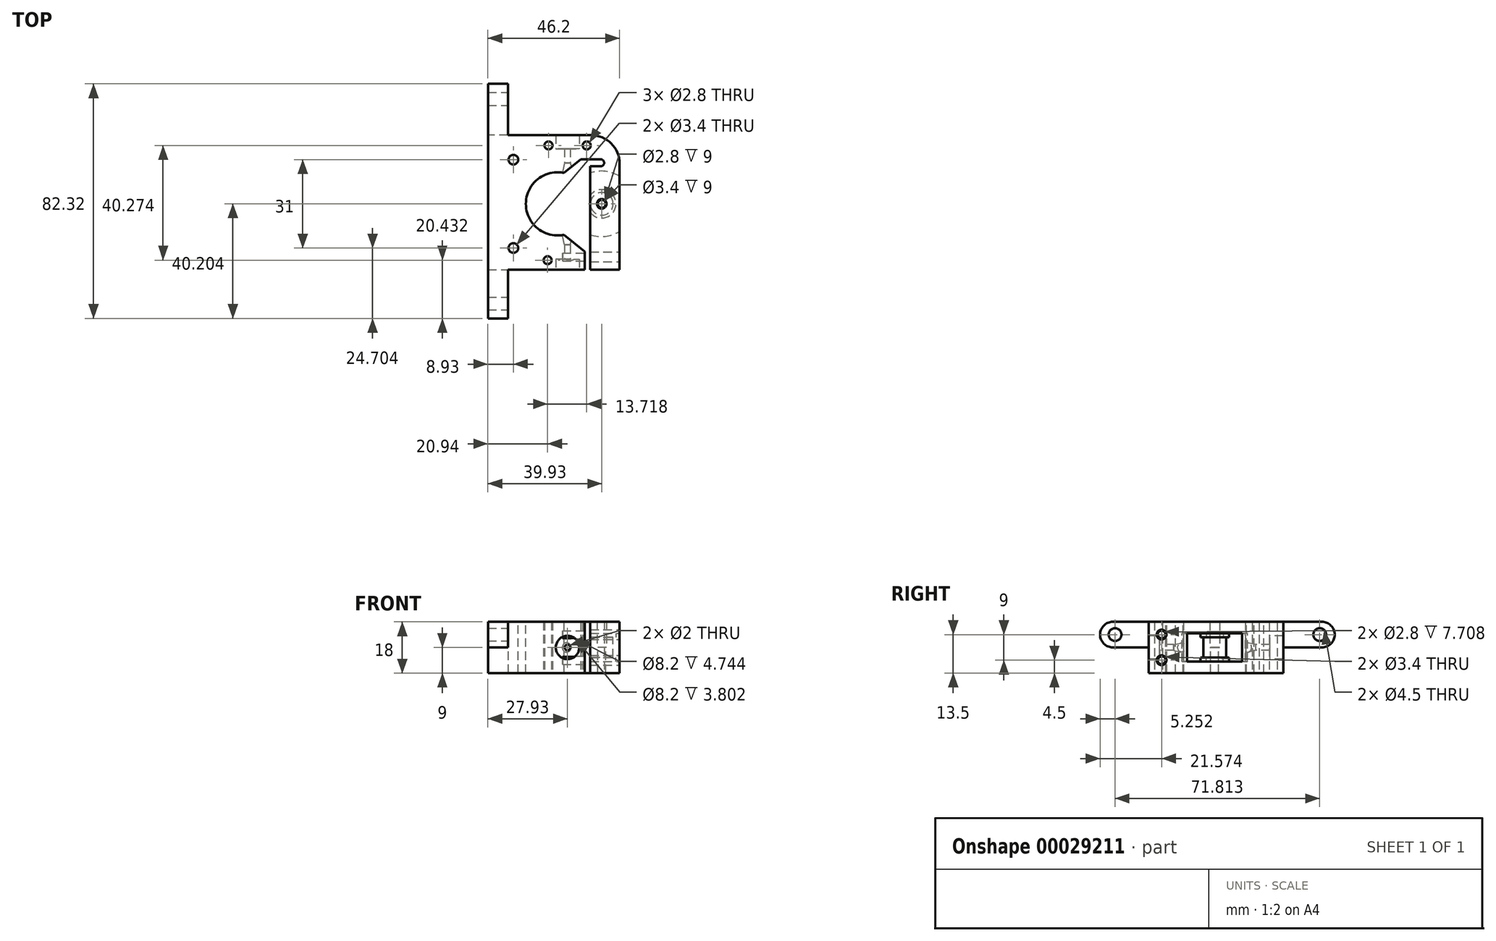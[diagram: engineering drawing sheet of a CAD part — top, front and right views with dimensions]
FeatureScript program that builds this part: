
annotation { "Feature Type Name" : "Feature", "Feature Type Description" : "" }
export const myFeature = defineFeature(function(context is Context, id is Id, definition is map)
    precondition{}
    {
        {
            var Q0;
            Q0=qCreatedBy(makeId("Top.planeOp"),FACE);
            var sketch = newSketch(context, id + "F0", { "sketchPlane" : qUnion([Q0])});
            skLineSegment(sketch, "E0", {"start": v(-24.43, 29.94) * mm, "end": v(-24.43, -17.36) * mm});
            skLineSegment(sketch, "E1", {"start": v(-24.43, -17.36) * mm, "end": v(-24.43, -17.36) * mm});
            skLineSegment(sketch, "E2", {"start": v(-24.43, -17.36) * mm, "end": v(-24.43, -17.35) * mm});
            skLineSegment(sketch, "E3", {"start": v(-24.43, -17.35) * mm, "end": v(9.48, -17.35) * mm});
            skLineSegment(sketch, "E4", {"start": v(9.48, -17.35) * mm, "end": v(9.48, 21.46) * mm});
            skLineSegment(sketch, "E5", {"start": v(9.48, 21.46) * mm, "end": v(15.14, 21.46) * mm});
            skLineSegment(sketch, "E6", {"start": v(15.14, 19) * mm, "end": v(11.48, 19) * mm});
            skLineSegment(sketch, "E7", {"start": v(11.48, 19) * mm, "end": v(11.48, -17.35) * mm});
            skLineSegment(sketch, "E8", {"start": v(11.48, -17.35) * mm, "end": v(21.77, -17.35) * mm});
            skLineSegment(sketch, "E9", {"start": v(21.77, -17.35) * mm, "end": v(21.77, 29.94) * mm});
            skLineSegment(sketch, "E10", {"start": v(21.77, 29.94) * mm, "end": v(-24.43, 29.94) * mm});
            skCircle(sketch, "E11", {"center": v(-3.17, 26.33) * mm, "radius": 1.4 * mm});
            skCircle(sketch, "E12", {"center": v(10.23, 26.33) * mm, "radius": 1.4 * mm});
            skCircle(sketch, "E13", {"center": v(-3.5, -13.95) * mm, "radius": 1.4 * mm});
            skArc(sketch, "E14", {"start": v(15.14, 19) * mm, "mid": v(16.36, 20.23) * mm, "end": v(15.14, 21.46) * mm});
            skSolve(sketch);
        }
        {
            var Q0;
            Q0=makeQuery(id+"F0.imprint","IMPRINT",FACE,{"disambiguationData":[TD([[makeQuery(id+"F0.imprint","IMPRINT",EDGE,{"derivedFrom":sQuery(id+"F0.wireOp",EDGE,"E0")}),1.0]])]});
            var Q1;
            Q1=makeQuery(id+"F0.imprint","IMPRINT",FACE,{"disambiguationData":[TD([[makeQuery(id+"F0.imprint","IMPRINT",EDGE,{"derivedFrom":sQuery(id+"F0.wireOp",EDGE,"E11")}),-1.0]])]});
            var Q2;
            Q2=makeQuery(id+"F0.imprint","IMPRINT",FACE,{"disambiguationData":[TD([[makeQuery(id+"F0.imprint","IMPRINT",EDGE,{"derivedFrom":sQuery(id+"F0.wireOp",EDGE,"E12")}),-1.0]])]});
            var Q3;
            Q3=makeQuery(id+"F0.imprint","IMPRINT",FACE,{"disambiguationData":[TD([[makeQuery(id+"F0.imprint","IMPRINT",EDGE,{"derivedFrom":sQuery(id+"F0.wireOp",EDGE,"E13")}),-1.0]])]});
            extrude(context, id + "F1", {"entities" : qUnion([Q0, Q1, Q2, Q3]), "depth" : 9 * mm});
        }
        {
            var Q0;
            Q0=makeQuery(id+"F1.opExtrude","CAP_FACE",FACE,{"disambiguationData":[OSD([sQuery(id+"F0.wireOp",EDGE,"E0"),sQuery(id+"F0.wireOp",EDGE,"E1"),sQuery(id+"F0.wireOp",EDGE,"E2"),sQuery(id+"F0.wireOp",EDGE,"E3"),sQuery(id+"F0.wireOp",EDGE,"E4"),sQuery(id+"F0.wireOp",EDGE,"E5"),sQuery(id+"F0.wireOp",EDGE,"E6"),sQuery(id+"F0.wireOp",EDGE,"E7"),sQuery(id+"F0.wireOp",EDGE,"E8"),sQuery(id+"F0.wireOp",EDGE,"E9"),sQuery(id+"F0.wireOp",EDGE,"E10"),sQuery(id+"F0.wireOp",EDGE,"604cad85-587a-4b7d-8070-06f4cba85480"),sQuery(id+"F0.wireOp",EDGE,"6e5e38c1-5bff-4efe-a8c5-b84022f0a049"),sQuery(id+"F0.wireOp",EDGE,"b8144507-9dd7-4af4-87a3-7b649dd00ae6"),sQuery(id+"F0.wireOp",EDGE,"b9c2cb7c-5e58-4995-888e-a78f0403fbb5"),sQuery(id+"F0.wireOp",EDGE,"885990ab-7576-4c23-8475-595d2769e284"),sQuery(id+"F0.wireOp",EDGE,"E11"),sQuery(id+"F0.wireOp",EDGE,"E12"),sQuery(id+"F0.wireOp",EDGE,"E13"),sQuery(id+"F0.wireOp",EDGE,"E14")])],"isStart":false});
            var sketch = newSketch(context, id + "F2", { "sketchPlane" : qUnion([Q0])});
            skCircle(sketch, "E15", {"center": v(0, 5.82) * mm, "radius": 11.1 * mm});
            skCircle(sketch, "E16", {"center": v(-15.5, 21.32) * mm, "radius": 1.7 * mm});
            skCircle(sketch, "E17", {"center": v(-15.5, -9.68) * mm, "radius": 1.7 * mm});
            skSolve(sketch);
        }
        {
            var Q0;
            Q0=qSketchRegion(id+"F2",true);
            extrude(context, id + "F3", {"entities" : qUnion([Q0]), "operationType" : NewBodyOperationType.REMOVE, "endBound" : BoundingType.THROUGH_ALL, "oppositeDirection" : true, "depth" : 25 * mm});
        }
        {
            var Q0;
            Q0=makeQuery(id+"F1.opExtrude","CAP_FACE",FACE,{"disambiguationData":[OSD([sQuery(id+"F0.wireOp",EDGE,"E0"),sQuery(id+"F0.wireOp",EDGE,"E1"),sQuery(id+"F0.wireOp",EDGE,"E2"),sQuery(id+"F0.wireOp",EDGE,"E3"),sQuery(id+"F0.wireOp",EDGE,"E4"),sQuery(id+"F0.wireOp",EDGE,"E5"),sQuery(id+"F0.wireOp",EDGE,"E6"),sQuery(id+"F0.wireOp",EDGE,"E7"),sQuery(id+"F0.wireOp",EDGE,"E8"),sQuery(id+"F0.wireOp",EDGE,"E9"),sQuery(id+"F0.wireOp",EDGE,"E10"),sQuery(id+"F0.wireOp",EDGE,"604cad85-587a-4b7d-8070-06f4cba85480"),sQuery(id+"F0.wireOp",EDGE,"6e5e38c1-5bff-4efe-a8c5-b84022f0a049"),sQuery(id+"F0.wireOp",EDGE,"E11"),sQuery(id+"F0.wireOp",EDGE,"E12"),sQuery(id+"F0.wireOp",EDGE,"E13"),sQuery(id+"F0.wireOp",EDGE,"E14")])],"isStart":false});
            var sketch = newSketch(context, id + "F4", { "sketchPlane" : qUnion([Q0])});
            skCircle(sketch, "E18", {"center": v(15.5, 5.82) * mm, "radius": 11.5 * mm});
            skCircle(sketch, "E19", {"center": v(15.5, 5.82) * mm, "radius": 5 * mm});
            skCircle(sketch, "E20", {"center": v(15.5, 5.82) * mm, "radius": 4 * mm});
            skLineSegment(sketch, "E21", {"start": v(0, 5.82) * mm, "end": v(31, 5.82) * mm, "construction": true});
            skCircle(sketch, "E22", {"center": v(15.5, 5.82) * mm, "radius": 1.4 * mm});
            skCircle(sketch, "E23", {"center": v(15.5, 5.82) * mm, "radius": 1.7 * mm});
            skSolve(sketch);
        }
        {
            var Q0;
            Q0=makeQuery(id+"F4.imprint","IMPRINT",FACE,{"disambiguationData":[TD([[makeQuery(id+"F4.imprint","IMPRINT",EDGE,{"derivedFrom":sQuery(id+"F4.wireOp",EDGE,"E19")}),-1.0]])]});
            extrude(context, id + "F5", {"entities" : qUnion([Q0]), "operationType" : NewBodyOperationType.REMOVE, "oppositeDirection" : true, "depth" : 5 * mm});
        }
        {
            var Q0;
            Q0=makeQuery(id+"F4.imprint","IMPRINT",FACE,{"disambiguationData":[TD([[makeQuery(id+"F4.imprint","IMPRINT",EDGE,{"derivedFrom":sQuery(id+"F4.wireOp",EDGE,"E19")}),1.0]])]});
            var Q1;
            Q1=makeQuery(id+"F4.imprint","IMPRINT",FACE,{"disambiguationData":[TD([[makeQuery(id+"F4.imprint","IMPRINT",EDGE,{"derivedFrom":sQuery(id+"F4.wireOp",EDGE,"E20")}),-1.0]])]});
            extrude(context, id + "F6", {"entities" : qUnion([Q0, Q1]), "operationType" : NewBodyOperationType.REMOVE, "oppositeDirection" : true, "depth" : 3.5 * mm});
        }
        {
            var Q0;
            {var subQ0=sQuery(id+"F0.wireOp",EDGE,"E0");var subQ1=sQuery(id+"F0.wireOp",EDGE,"E1");var subQ2=sQuery(id+"F0.wireOp",EDGE,"E2");var subQ3=sQuery(id+"F0.wireOp",EDGE,"E3");var subQ4=sQuery(id+"F0.wireOp",EDGE,"E4");var subQ5=sQuery(id+"F0.wireOp",EDGE,"E5");var subQ6=sQuery(id+"F0.wireOp",EDGE,"E6");var subQ7=sQuery(id+"F0.wireOp",EDGE,"E7");var subQ8=sQuery(id+"F0.wireOp",EDGE,"E9");var subQ9=sQuery(id+"F0.wireOp",EDGE,"E10");var subQ10=sQuery(id+"F0.wireOp",EDGE,"604cad85-587a-4b7d-8070-06f4cba85480");var subQ11=sQuery(id+"F0.wireOp",EDGE,"6e5e38c1-5bff-4efe-a8c5-b84022f0a049");var subQ12=sQuery(id+"F0.wireOp",EDGE,"E11");var subQ13=sQuery(id+"F0.wireOp",EDGE,"E12");var subQ14=sQuery(id+"F0.wireOp",EDGE,"E13");var subQ15=sQuery(id+"F0.wireOp",EDGE,"E14");Q0=makeQuery(id+"F5.boolean.opBoolean","SPLIT",FACE,{"disambiguationData":[TD([makeQuery(id+"F1.opExtrude","SWEPT_FACE",FACE,{"disambiguationData":[OSD([subQ0])]})])],"derivedFrom":makeQuery(id+"F1.opExtrude","CAP_FACE",FACE,{"disambiguationData":[OSD([subQ0,subQ1,subQ2,subQ3,subQ4,subQ5,subQ6,subQ7,sQuery(id+"F0.wireOp",EDGE,"E8"),subQ8,subQ9,subQ10,subQ11,subQ12,subQ13,subQ14,subQ15])],"isStart":false})});}
            var sketch = newSketch(context, id + "F7", { "sketchPlane" : qUnion([Q0])});
            skLineSegment(sketch, "E24", {"start": v(-0.6, 30.2) * mm, "end": v(-0.6, 25.2) * mm});
            skLineSegment(sketch, "E25", {"start": v(-0.6, 25.2) * mm, "end": v(2.5, 25.2) * mm});
            skLineSegment(sketch, "E26", {"start": v(2.5, 25.2) * mm, "end": v(2.5, 20.21) * mm});
            skLineSegment(sketch, "E27", {"start": v(2.5, 20.21) * mm, "end": v(1.31, 15.18) * mm});
            skLineSegment(sketch, "E28", {"start": v(1.31, 15.18) * mm, "end": v(3.5, 15.18) * mm});
            skLineSegment(sketch, "E29", {"start": v(3.5, 15.18) * mm, "end": v(3.5, 30.2) * mm});
            skLineSegment(sketch, "E30", {"start": v(3.5, 30.2) * mm, "end": v(-0.6, 30.2) * mm});
            skLineSegment(sketch, "E31", {"start": v(0, 5.82) * mm, "end": v(31.4, 5.82) * mm, "construction": true});
            skLineSegment(sketch, "E32.0.MirrorCS", {"start": v(-0.6, -13.54) * mm, "end": v(2.5, -13.54) * mm});
            skLineSegment(sketch, "E32.1.MirrorCS", {"start": v(3.5, -3.53) * mm, "end": v(3.5, -18.54) * mm});
            skLineSegment(sketch, "E32.2.MirrorCS", {"start": v(-0.6, -18.54) * mm, "end": v(-0.6, -13.54) * mm});
            skLineSegment(sketch, "E32.3.MirrorCS", {"start": v(1.31, -3.53) * mm, "end": v(3.5, -3.53) * mm});
            skLineSegment(sketch, "E32.4.MirrorCS", {"start": v(2.5, -8.56) * mm, "end": v(1.31, -3.53) * mm});
            skLineSegment(sketch, "E32.5.MirrorCS", {"start": v(2.5, -13.54) * mm, "end": v(2.5, -8.56) * mm});
            skLineSegment(sketch, "E32.6.MirrorCS", {"start": v(3.5, -18.54) * mm, "end": v(-0.6, -18.54) * mm});
            skSolve(sketch);
        }
        {
            var Q0;
            Q0=qSketchRegion(id+"F7",true);
            var Q1;
            Q1=sQuery(id+"F7.wireOp",EDGE,"E29");
            revolve(context, id + "F8", {"entities" : qUnion([Q0]), "axis" : qUnion([Q1]), "revolveType" : RevolveType.FULL});
        }
        {
            var Q0;
            Q0=makeQuery(id+"F8.opRevolve","SWEPT_BODY",BODY,{"disambiguationData":[OSD([sQuery(id+"F7.wireOp",EDGE,"E24"),sQuery(id+"F7.wireOp",EDGE,"E25"),sQuery(id+"F7.wireOp",EDGE,"E26"),sQuery(id+"F7.wireOp",EDGE,"E27"),sQuery(id+"F7.wireOp",EDGE,"E28"),sQuery(id+"F7.wireOp",EDGE,"E29"),sQuery(id+"F7.wireOp",EDGE,"E30")])]});
            var Q1;
            Q1=makeQuery(id+"F1.opExtrude","SWEPT_BODY",BODY,{"disambiguationData":[OSD([sQuery(id+"F0.wireOp",EDGE,"E0"),sQuery(id+"F0.wireOp",EDGE,"E1"),sQuery(id+"F0.wireOp",EDGE,"E2"),sQuery(id+"F0.wireOp",EDGE,"E3"),sQuery(id+"F0.wireOp",EDGE,"E4"),sQuery(id+"F0.wireOp",EDGE,"E5"),sQuery(id+"F0.wireOp",EDGE,"E6"),sQuery(id+"F0.wireOp",EDGE,"E7"),sQuery(id+"F0.wireOp",EDGE,"E8"),sQuery(id+"F0.wireOp",EDGE,"E9"),sQuery(id+"F0.wireOp",EDGE,"E10"),sQuery(id+"F0.wireOp",EDGE,"604cad85-587a-4b7d-8070-06f4cba85480"),sQuery(id+"F0.wireOp",EDGE,"6e5e38c1-5bff-4efe-a8c5-b84022f0a049"),sQuery(id+"F0.wireOp",EDGE,"E11"),sQuery(id+"F0.wireOp",EDGE,"E12"),sQuery(id+"F0.wireOp",EDGE,"E13"),sQuery(id+"F0.wireOp",EDGE,"E14")])]});
            booleanBodies(context, id + "F9", {"operationType" : BooleanOperationType.SUBTRACTION, "tools" : qUnion([Q0]), "targets" : qUnion([Q1]), "keepTools" : true});
        }
        {
            var Q0;
            Q0=makeQuery(id+"F8.opRevolve","SWEPT_BODY",BODY,{"disambiguationData":[OSD([sQuery(id+"F7.wireOp",EDGE,"E32.0.MirrorCS"),sQuery(id+"F7.wireOp",EDGE,"E32.1.MirrorCS"),sQuery(id+"F7.wireOp",EDGE,"E32.2.MirrorCS"),sQuery(id+"F7.wireOp",EDGE,"E32.3.MirrorCS"),sQuery(id+"F7.wireOp",EDGE,"E32.4.MirrorCS"),sQuery(id+"F7.wireOp",EDGE,"E32.5.MirrorCS"),sQuery(id+"F7.wireOp",EDGE,"E32.6.MirrorCS")])]});
            var Q1;
            Q1=makeQuery(id+"F1.opExtrude","SWEPT_BODY",BODY,{"disambiguationData":[OSD([sQuery(id+"F0.wireOp",EDGE,"E0"),sQuery(id+"F0.wireOp",EDGE,"E1"),sQuery(id+"F0.wireOp",EDGE,"E2"),sQuery(id+"F0.wireOp",EDGE,"E3"),sQuery(id+"F0.wireOp",EDGE,"E4"),sQuery(id+"F0.wireOp",EDGE,"E5"),sQuery(id+"F0.wireOp",EDGE,"E6"),sQuery(id+"F0.wireOp",EDGE,"E7"),sQuery(id+"F0.wireOp",EDGE,"E8"),sQuery(id+"F0.wireOp",EDGE,"E9"),sQuery(id+"F0.wireOp",EDGE,"E10"),sQuery(id+"F0.wireOp",EDGE,"604cad85-587a-4b7d-8070-06f4cba85480"),sQuery(id+"F0.wireOp",EDGE,"6e5e38c1-5bff-4efe-a8c5-b84022f0a049"),sQuery(id+"F0.wireOp",EDGE,"E11"),sQuery(id+"F0.wireOp",EDGE,"E12"),sQuery(id+"F0.wireOp",EDGE,"E13"),sQuery(id+"F0.wireOp",EDGE,"E14")])]});
            booleanBodies(context, id + "F10", {"operationType" : BooleanOperationType.SUBTRACTION, "tools" : qUnion([Q0]), "targets" : qUnion([Q1]), "keepTools" : true});
        }
        {
            var Q0;
            Q0=makeQuery(id+"F1.opExtrude","SWEPT_EDGE",EDGE,{"disambiguationData":[OSD([sQuery(id+"F0.wireOp",EDGE,"E9"),sQuery(id+"F0.wireOp",EDGE,"E10")])]});
            fillet(context, id + "F11", {"entities" : qUnion([Q0]), "radius" : 10 * mm, "tangentPropagation" : true, "allowEdgeOverflow" : false});
        }
        {
            var Q0;
            Q0=qSketchRegion(id+"F0",true);
            extrude(context, id + "F12", {"entities" : qUnion([Q0]), "oppositeDirection" : true, "depth" : 9 * mm});
        }
        {
            var Q0;
            Q0=makeQuery(id+"F12.opExtrude","SWEPT_BODY",BODY,{"disambiguationData":[OSD([sQuery(id+"F0.wireOp",EDGE,"E0"),sQuery(id+"F0.wireOp",EDGE,"E3"),sQuery(id+"F0.wireOp",EDGE,"E4"),sQuery(id+"F0.wireOp",EDGE,"E5"),sQuery(id+"F0.wireOp",EDGE,"E6"),sQuery(id+"F0.wireOp",EDGE,"E7"),sQuery(id+"F0.wireOp",EDGE,"E8"),sQuery(id+"F0.wireOp",EDGE,"E9"),sQuery(id+"F0.wireOp",EDGE,"E10"),sQuery(id+"F0.wireOp",EDGE,"E11"),sQuery(id+"F0.wireOp",EDGE,"E12"),sQuery(id+"F0.wireOp",EDGE,"E13"),sQuery(id+"F0.wireOp",EDGE,"E14")])]});
            transform(context, id + "F13", {"entities" : qUnion([Q0]), "transformType" : TransformType.TRANSLATION_3D, "dx" : 0 * mm, "dy" : 0 * mm, "dz" : 18 * mm, "makeCopy" : false});
        }
        {
            var Q0;
            Q0=makeQuery(id+"F12.opExtrude","SWEPT_EDGE",EDGE,{"disambiguationData":[OSD([sQuery(id+"F0.wireOp",EDGE,"E9"),sQuery(id+"F0.wireOp",EDGE,"E10")])]});
            fillet(context, id + "F14", {"entities" : qUnion([Q0]), "radius" : 10 * mm, "tangentPropagation" : true, "allowEdgeOverflow" : false});
        }
        {
            var Q0;
            Q0=qSketchRegion(id+"F2",true);
            extrude(context, id + "F15", {"entities" : qUnion([Q0]), "operationType" : NewBodyOperationType.REMOVE, "endBound" : BoundingType.THROUGH_ALL, "depth" : 25 * mm});
        }
        {
            var Q0;
            {var subQ3=sQuery(id+"F4.wireOp",EDGE,"E18");var subQ7=makeQuery(id+"F1.opExtrude","CAP_EDGE",EDGE,{"disambiguationData":[OSD([sQuery(id+"F0.wireOp",EDGE,"E9")])],"isStart":false});var subQ9=makeQuery(id+"F4.imprint","INTERSECT",VERTEX,{"disambiguationData":[OD(0.0)],"derivedFrom":[subQ7,subQ3]});Q0=makeQuery(id+"F4.imprint","IMPRINT",FACE,{"disambiguationData":[TD([[makeQuery(id+"F4.imprint","IMPRINT",EDGE,{"disambiguationData":[TD([[subQ9,-1.0]])],"derivedFrom":subQ3}),1.0]])]});}
            extrude(context, id + "F16", {"entities" : qUnion([Q0]), "operationType" : NewBodyOperationType.REMOVE, "depth" : 5 * mm});
        }
        {
            var Q0;
            Q0=makeQuery(id+"F4.imprint","IMPRINT",FACE,{"disambiguationData":[TD([[makeQuery(id+"F4.imprint","IMPRINT",EDGE,{"derivedFrom":sQuery(id+"F4.wireOp",EDGE,"E20")}),-1.0]])]});
            extrude(context, id + "F17", {"entities" : qUnion([Q0]), "operationType" : NewBodyOperationType.REMOVE, "depth" : 3.5 * mm});
        }
        {
            var Q0;
            Q0=makeQuery(id+"F8.opRevolve","SWEPT_BODY",BODY,{"disambiguationData":[OSD([sQuery(id+"F7.wireOp",EDGE,"E24"),sQuery(id+"F7.wireOp",EDGE,"E25"),sQuery(id+"F7.wireOp",EDGE,"E26"),sQuery(id+"F7.wireOp",EDGE,"E27"),sQuery(id+"F7.wireOp",EDGE,"E28"),sQuery(id+"F7.wireOp",EDGE,"E29"),sQuery(id+"F7.wireOp",EDGE,"E30")])]});
            var Q1;
            Q1=makeQuery(id+"F12.opExtrude","SWEPT_BODY",BODY,{"disambiguationData":[OSD([sQuery(id+"F0.wireOp",EDGE,"E0"),sQuery(id+"F0.wireOp",EDGE,"E3"),sQuery(id+"F0.wireOp",EDGE,"E4"),sQuery(id+"F0.wireOp",EDGE,"E5"),sQuery(id+"F0.wireOp",EDGE,"E6"),sQuery(id+"F0.wireOp",EDGE,"E7"),sQuery(id+"F0.wireOp",EDGE,"E8"),sQuery(id+"F0.wireOp",EDGE,"E9"),sQuery(id+"F0.wireOp",EDGE,"E10"),sQuery(id+"F0.wireOp",EDGE,"E11"),sQuery(id+"F0.wireOp",EDGE,"E12"),sQuery(id+"F0.wireOp",EDGE,"E13"),sQuery(id+"F0.wireOp",EDGE,"E14")])]});
            booleanBodies(context, id + "F18", {"operationType" : BooleanOperationType.SUBTRACTION, "tools" : qUnion([Q0]), "targets" : qUnion([Q1])});
        }
        {
            var Q0;
            Q0=makeQuery(id+"F8.opRevolve","SWEPT_BODY",BODY,{"disambiguationData":[OSD([sQuery(id+"F7.wireOp",EDGE,"E32.0.MirrorCS"),sQuery(id+"F7.wireOp",EDGE,"E32.1.MirrorCS"),sQuery(id+"F7.wireOp",EDGE,"E32.2.MirrorCS"),sQuery(id+"F7.wireOp",EDGE,"E32.3.MirrorCS"),sQuery(id+"F7.wireOp",EDGE,"E32.4.MirrorCS"),sQuery(id+"F7.wireOp",EDGE,"E32.5.MirrorCS"),sQuery(id+"F7.wireOp",EDGE,"E32.6.MirrorCS")])]});
            var Q1;
            Q1=makeQuery(id+"F12.opExtrude","SWEPT_BODY",BODY,{"disambiguationData":[OSD([sQuery(id+"F0.wireOp",EDGE,"E0"),sQuery(id+"F0.wireOp",EDGE,"E3"),sQuery(id+"F0.wireOp",EDGE,"E4"),sQuery(id+"F0.wireOp",EDGE,"E5"),sQuery(id+"F0.wireOp",EDGE,"E6"),sQuery(id+"F0.wireOp",EDGE,"E7"),sQuery(id+"F0.wireOp",EDGE,"E8"),sQuery(id+"F0.wireOp",EDGE,"E9"),sQuery(id+"F0.wireOp",EDGE,"E10"),sQuery(id+"F0.wireOp",EDGE,"E11"),sQuery(id+"F0.wireOp",EDGE,"E12"),sQuery(id+"F0.wireOp",EDGE,"E13"),sQuery(id+"F0.wireOp",EDGE,"E14")])]});
            booleanBodies(context, id + "F19", {"operationType" : BooleanOperationType.SUBTRACTION, "tools" : qUnion([Q0]), "targets" : qUnion([Q1])});
        }
        {
            var Q0;
            Q0=makeQuery(id+"F12.opExtrude","SWEPT_FACE",FACE,{"disambiguationData":[OSD([sQuery(id+"F0.wireOp",EDGE,"E9")])]});
            var sketch = newSketch(context, id + "F20", { "sketchPlane" : qUnion([Q0])});
            skCircle(sketch, "E33", {"center": v(-12.8, 13.5) * mm, "radius": 1.7 * mm});
            skCircle(sketch, "E34", {"center": v(-12.8, 13.5) * mm, "radius": 1.4 * mm});
            skCircle(sketch, "E35", {"center": v(-12.8, 4.5) * mm, "radius": 1.7 * mm});
            skCircle(sketch, "E36", {"center": v(-12.8, 4.5) * mm, "radius": 1.4 * mm});
            skSolve(sketch);
        }
        {
            var Q0;
            Q0=makeQuery(id+"F20.imprint","IMPRINT",FACE,{"disambiguationData":[TD([[makeQuery(id+"F20.imprint","IMPRINT",EDGE,{"derivedFrom":sQuery(id+"F20.wireOp",EDGE,"E34")}),1.0]])]});
            extrude(context, id + "F21", {"entities" : qUnion([Q0]), "operationType" : NewBodyOperationType.REMOVE, "oppositeDirection" : true, "depth" : 20 * mm});
        }
        {
            var Q0;
            Q0=makeQuery(id+"F20.imprint","IMPRINT",FACE,{"disambiguationData":[TD([[makeQuery(id+"F20.imprint","IMPRINT",EDGE,{"derivedFrom":sQuery(id+"F20.wireOp",EDGE,"E33")}),1.0]])]});
            extrude(context, id + "F22", {"entities" : qUnion([Q0]), "operationType" : NewBodyOperationType.REMOVE, "oppositeDirection" : true, "depth" : 11 * mm});
        }
        {
            var Q0;
            Q0=makeQuery(id+"F20.imprint","IMPRINT",FACE,{"disambiguationData":[TD([[makeQuery(id+"F20.imprint","IMPRINT",EDGE,{"derivedFrom":sQuery(id+"F20.wireOp",EDGE,"E36")}),1.0]])]});
            extrude(context, id + "F23", {"entities" : qUnion([Q0]), "operationType" : NewBodyOperationType.REMOVE, "oppositeDirection" : true, "depth" : 20 * mm});
        }
        {
            var Q0;
            Q0=makeQuery(id+"F20.imprint","IMPRINT",FACE,{"disambiguationData":[TD([[makeQuery(id+"F20.imprint","IMPRINT",EDGE,{"derivedFrom":sQuery(id+"F20.wireOp",EDGE,"E35")}),1.0]])]});
            extrude(context, id + "F24", {"entities" : qUnion([Q0]), "operationType" : NewBodyOperationType.REMOVE, "oppositeDirection" : true, "depth" : 11 * mm});
        }
        {
            var Q0;
            Q0=makeQuery(id+"F4.imprint","IMPRINT",FACE,{"disambiguationData":[TD([[makeQuery(id+"F4.imprint","IMPRINT",EDGE,{"derivedFrom":sQuery(id+"F4.wireOp",EDGE,"E22")}),1.0]])]});
            extrude(context, id + "F25", {"entities" : qUnion([Q0]), "operationType" : NewBodyOperationType.REMOVE, "endBound" : BoundingType.THROUGH_ALL, "oppositeDirection" : true, "depth" : 25 * mm});
        }
        {
            var Q0;
            Q0=makeQuery(id+"F4.imprint","IMPRINT",FACE,{"disambiguationData":[TD([[makeQuery(id+"F4.imprint","IMPRINT",EDGE,{"derivedFrom":sQuery(id+"F4.wireOp",EDGE,"E22")}),1.0]])]});
            var Q1;
            Q1=makeQuery(id+"F4.imprint","IMPRINT",FACE,{"disambiguationData":[TD([[makeQuery(id+"F4.imprint","IMPRINT",EDGE,{"derivedFrom":sQuery(id+"F4.wireOp",EDGE,"E22")}),-1.0]])]});
            extrude(context, id + "F26", {"entities" : qUnion([Q0, Q1]), "operationType" : NewBodyOperationType.REMOVE, "endBound" : BoundingType.THROUGH_ALL, "depth" : 25 * mm});
        }
        {
            var Q0;
            Q0=makeQuery(id+"F12.opExtrude","SWEPT_FACE",FACE,{"disambiguationData":[OSD([sQuery(id+"F0.wireOp",EDGE,"E10")])]});
            var sketch = newSketch(context, id + "F27", { "sketchPlane" : qUnion([Q0])});
            skLineSegment(sketch, "E37.bottom", {"start": v(24.43, 9) * mm, "end": v(17.43, 9) * mm});
            skLineSegment(sketch, "E37.top", {"start": v(24.43, 18) * mm, "end": v(17.43, 18) * mm});
            skLineSegment(sketch, "E37.left", {"start": v(24.43, 9) * mm, "end": v(24.43, 18) * mm});
            skLineSegment(sketch, "E37.right", {"start": v(17.43, 9) * mm, "end": v(17.43, 18) * mm});
            skSolve(sketch);
        }
        {
            var Q0;
            Q0=qSketchRegion(id+"F27",true);
            extrude(context, id + "F28", {"entities" : qUnion([Q0]), "operationType" : NewBodyOperationType.ADD, "depth" : 18 * mm, "hasSecondDirection" : true, "secondDirectionOppositeDirection" : true, "secondDirectionDepth" : 64.31 * mm});
        }
        {
            var Q0;
            {var subQ0=sQuery(id+"F27.wireOp",EDGE,"E37.right");var subQ3=sQuery(id+"F0.wireOp",EDGE,"E3");Q0=makeQuery(id+"F28.boolean.opBoolean","SPLIT",FACE,{"disambiguationData":[TD([makeQuery(id+"F12.opExtrude","SWEPT_FACE",FACE,{"disambiguationData":[OSD([subQ3])]})])],"derivedFrom":makeQuery(id+"F28.opExtrude","SWEPT_FACE",FACE,{"disambiguationData":[OSD([subQ0])]})});}
            var sketch = newSketch(context, id + "F29", { "sketchPlane" : qUnion([Q0])});
            skCircle(sketch, "E38", {"center": v(-29.13, 13.5) * mm, "radius": 2.25 * mm});
            skPoint(sketch, "E39", {"position": v(-34.38, 13.5) * mm});
            skSolve(sketch);
        }
        {
            var Q0;
            {var subQ0=sQuery(id+"F27.wireOp",EDGE,"E37.right");var subQ3=sQuery(id+"F0.wireOp",EDGE,"E10");Q0=makeQuery(id+"F28.boolean.opBoolean","SPLIT",FACE,{"disambiguationData":[TD([makeQuery(id+"F12.opExtrude","SWEPT_FACE",FACE,{"disambiguationData":[OSD([subQ3])]})])],"derivedFrom":makeQuery(id+"F28.opExtrude","SWEPT_FACE",FACE,{"disambiguationData":[OSD([subQ0])]})});}
            var sketch = newSketch(context, id + "F30", { "sketchPlane" : qUnion([Q0])});
            skCircle(sketch, "E40", {"center": v(42.69, 13.5) * mm, "radius": 2.25 * mm});
            skPoint(sketch, "E41", {"position": v(47.94, 13.5) * mm});
            skSolve(sketch);
        }
        {
            var Q0;
            Q0=qSketchRegion(id+"F29",true);
            var Q1;
            Q1=qSketchRegion(id+"F30",true);
            extrude(context, id + "F31", {"entities" : qUnion([Q0, Q1]), "operationType" : NewBodyOperationType.REMOVE, "oppositeDirection" : true, "depth" : 25 * mm});
        }
        {
            var Q0;
            Q0=makeQuery(id+"F28.opExtrude","CAP_EDGE",EDGE,{"disambiguationData":[OSD([sQuery(id+"F27.wireOp",EDGE,"E37.top")])],"isStart":true});
            var Q1;
            Q1=makeQuery(id+"F28.opExtrude","CAP_EDGE",EDGE,{"disambiguationData":[OSD([sQuery(id+"F27.wireOp",EDGE,"E37.bottom")])],"isStart":true});
            var Q2;
            Q2=makeQuery(id+"F28.opExtrude","CAP_EDGE",EDGE,{"disambiguationData":[OSD([sQuery(id+"F27.wireOp",EDGE,"E37.top")])],"isStart":false});
            var Q3;
            Q3=makeQuery(id+"F28.opExtrude","CAP_EDGE",EDGE,{"disambiguationData":[OSD([sQuery(id+"F27.wireOp",EDGE,"E37.bottom")])],"isStart":false});
            fillet(context, id + "F32", {"entities" : qUnion([Q0, Q1, Q2, Q3]), "radius" : 4.5 * mm, "tangentPropagation" : true, "allowEdgeOverflow" : false});
        }
        {
            var Q0;
            Q0=makeQuery(id+"F3.boolean.opBoolean","INTERSECT",EDGE,{"disambiguationData":[OD(0.0)],"derivedFrom":[makeQuery(id+"F1.opExtrude","SWEPT_FACE",FACE,{"disambiguationData":[OSD([sQuery(id+"F0.wireOp",EDGE,"E4")])]}),makeQuery(id+"F3.opExtrude","SWEPT_FACE",FACE,{"disambiguationData":[OSD([sQuery(id+"F2.wireOp",EDGE,"E15")])]})]});
            var Q1;
            Q1=makeQuery(id+"F3.boolean.opBoolean","INTERSECT",EDGE,{"disambiguationData":[OD(1.0)],"derivedFrom":[makeQuery(id+"F1.opExtrude","SWEPT_FACE",FACE,{"disambiguationData":[OSD([sQuery(id+"F0.wireOp",EDGE,"E4")])]}),makeQuery(id+"F3.opExtrude","SWEPT_FACE",FACE,{"disambiguationData":[OSD([sQuery(id+"F2.wireOp",EDGE,"E15")])]})]});
            var Q2;
            Q2=makeQuery(id+"F15.boolean.opBoolean","INTERSECT",EDGE,{"disambiguationData":[OD(1.0)],"derivedFrom":[makeQuery(id+"F12.opExtrude","SWEPT_FACE",FACE,{"disambiguationData":[OSD([sQuery(id+"F0.wireOp",EDGE,"E4")])]}),makeQuery(id+"F15.opExtrude","SWEPT_FACE",FACE,{"disambiguationData":[OSD([sQuery(id+"F2.wireOp",EDGE,"E15")])]})]});
            var Q3;
            Q3=makeQuery(id+"F15.boolean.opBoolean","INTERSECT",EDGE,{"disambiguationData":[OD(0.0)],"derivedFrom":[makeQuery(id+"F12.opExtrude","SWEPT_FACE",FACE,{"disambiguationData":[OSD([sQuery(id+"F0.wireOp",EDGE,"E4")])]}),makeQuery(id+"F15.opExtrude","SWEPT_FACE",FACE,{"disambiguationData":[OSD([sQuery(id+"F2.wireOp",EDGE,"E15")])]})]});
            chamfer(context, id + "F33", {"entities" : qUnion([Q0, Q1, Q2, Q3]), "width" : 6 * mm, "tangentPropagation" : true});
        }
    });
